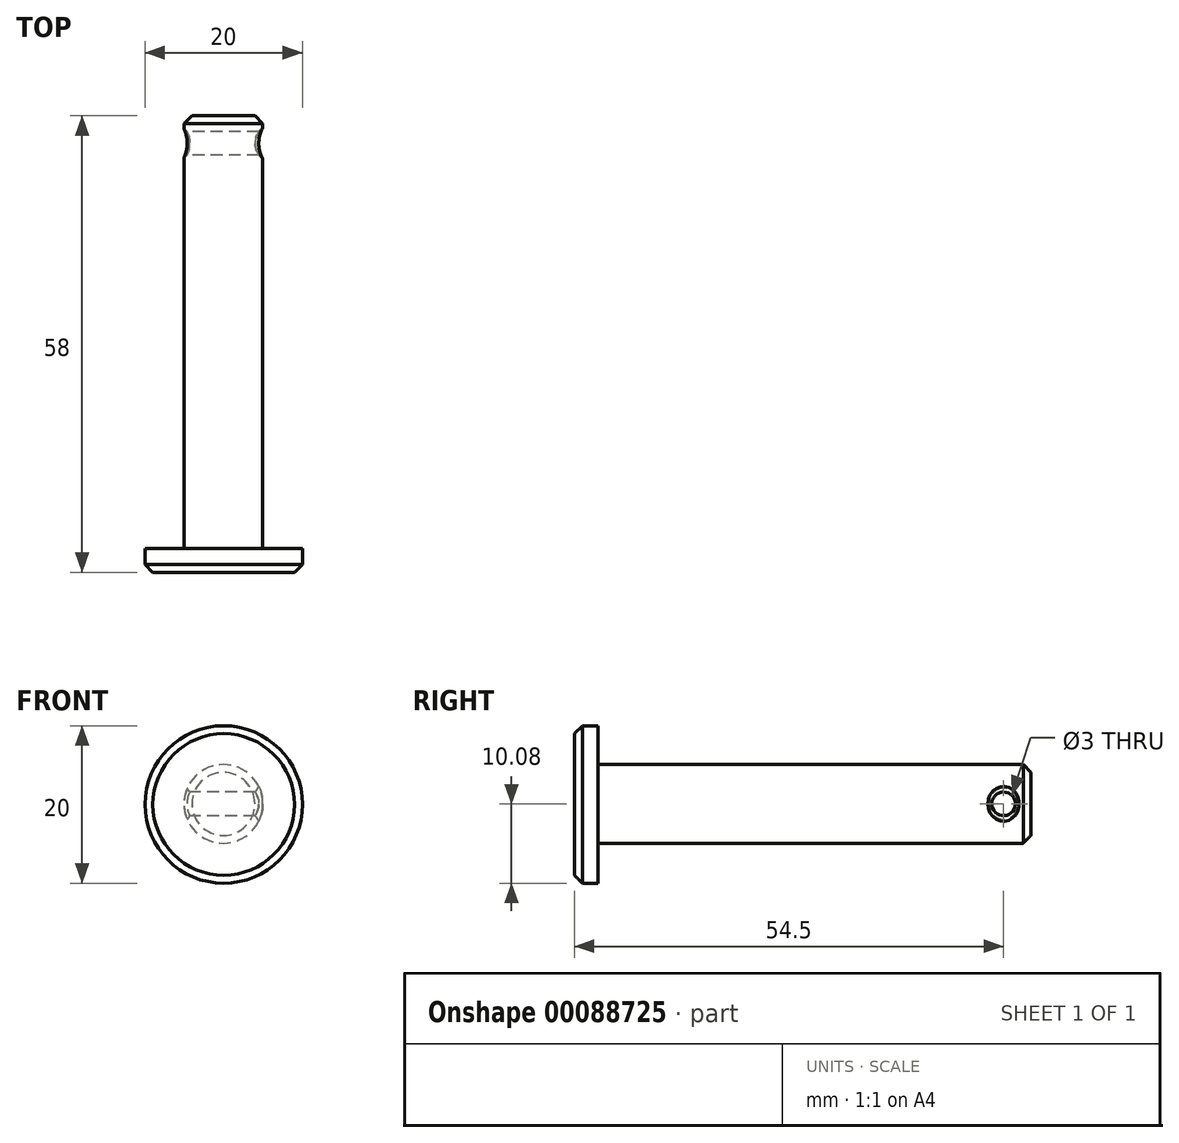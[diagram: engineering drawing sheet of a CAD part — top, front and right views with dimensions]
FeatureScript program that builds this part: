
annotation { "Feature Type Name" : "Feature", "Feature Type Description" : "" }
export const myFeature = defineFeature(function(context is Context, id is Id, definition is map)
    precondition{}
    {
        {
            var Q0;
            Q0=qCreatedBy(makeId("Front.planeOp"),FACE);
            var sketch = newSketch(context, id + "F0", { "sketchPlane" : qUnion([Q0])});
            skCircle(sketch, "E0", {"center": v(0, 0) * mm, "radius": 5 * mm});
            skCircle(sketch, "E1", {"center": v(0.04, -0.08) * mm, "radius": 10 * mm});
            skSolve(sketch);
        }
        {
            var Q0;
            Q0 = qSketchRegion(id + "F0", true);
            var Q1;
            Q1=makeQuery(id+"F0.imprint","IMPRINT",FACE,{"disambiguationData":[TD([[makeQuery(id+"F0.imprint","IMPRINT",EDGE,{"derivedFrom":sQuery(id+"F0.wireOp",EDGE,"E0")}),1.0]])]});
            extrude(context, id + "F1", {"entities" : qUnion([Q0, Q1]), "depth" : 3 * mm});
        }
        {
            var Q0;
            Q0=makeQuery(id+"F0.imprint","IMPRINT",FACE,{"disambiguationData":[TD([[makeQuery(id+"F0.imprint","IMPRINT",EDGE,{"derivedFrom":sQuery(id+"F0.wireOp",EDGE,"E0")}),1.0]])]});
            extrude(context, id + "F2", {"entities" : qUnion([Q0]), "operationType" : NewBodyOperationType.ADD, "oppositeDirection" : true, "depth" : 55 * mm});
        }
        {
            var Q0;
            Q0=makeQuery(id+"F1.opExtrude","CAP_EDGE",EDGE,{"disambiguationData":[OSD([sQuery(id+"F0.wireOp",EDGE,"E1")])],"isStart":false});
            var Q1;
            Q1=makeQuery(id+"F2.opExtrude","CAP_EDGE",EDGE,{"disambiguationData":[OSD([sQuery(id+"F0.wireOp",EDGE,"E0")])],"isStart":false});
            chamfer(context, id + "F3", {"entities" : qUnion([Q0, Q1]), "width" : 1 * mm, "tangentPropagation" : true});
        }
        {
            var Q0;
            Q0=qCreatedBy(makeId("Right.planeOp"),FACE);
            var sketch = newSketch(context, id + "F4", { "sketchPlane" : qUnion([Q0])});
            skPoint(sketch, "E2", {"position": v(51.5, 0) * mm});
            skCircle(sketch, "E3", {"center": v(51.5, 0) * mm, "radius": 1.5 * mm});
            skSolve(sketch);
        }
        {
            var Q0;
            Q0 = qSketchRegion(id + "F4", true);
            extrude(context, id + "F5", {"entities" : qUnion([Q0]), "operationType" : NewBodyOperationType.REMOVE, "depth" : 10 * mm, "symmetric" : true});
        }
        {
            var Q0;
            Q0=makeQuery(id+"F5.boolean.opBoolean","INTERSECT",EDGE,{"disambiguationData":[OD(1.0)],"derivedFrom":[makeQuery(id+"F2.opExtrude","SWEPT_FACE",FACE,{"disambiguationData":[OSD([sQuery(id+"F0.wireOp",EDGE,"E0")])]}),makeQuery(id+"F5.opExtrude","SWEPT_FACE",FACE,{"disambiguationData":[OSD([sQuery(id+"F4.wireOp",EDGE,"E3")])]})]});
            var Q1;
            Q1=makeQuery(id+"F5.boolean.opBoolean","INTERSECT",EDGE,{"disambiguationData":[OD(0.0)],"derivedFrom":[makeQuery(id+"F2.opExtrude","SWEPT_FACE",FACE,{"disambiguationData":[OSD([sQuery(id+"F0.wireOp",EDGE,"E0")])]}),makeQuery(id+"F5.opExtrude","SWEPT_FACE",FACE,{"disambiguationData":[OSD([sQuery(id+"F4.wireOp",EDGE,"E3")])]})]});
            chamfer(context, id + "F6", {"entities" : qUnion([Q0, Q1]), "width" : 0.5 * mm, "tangentPropagation" : true});
        }
    });
